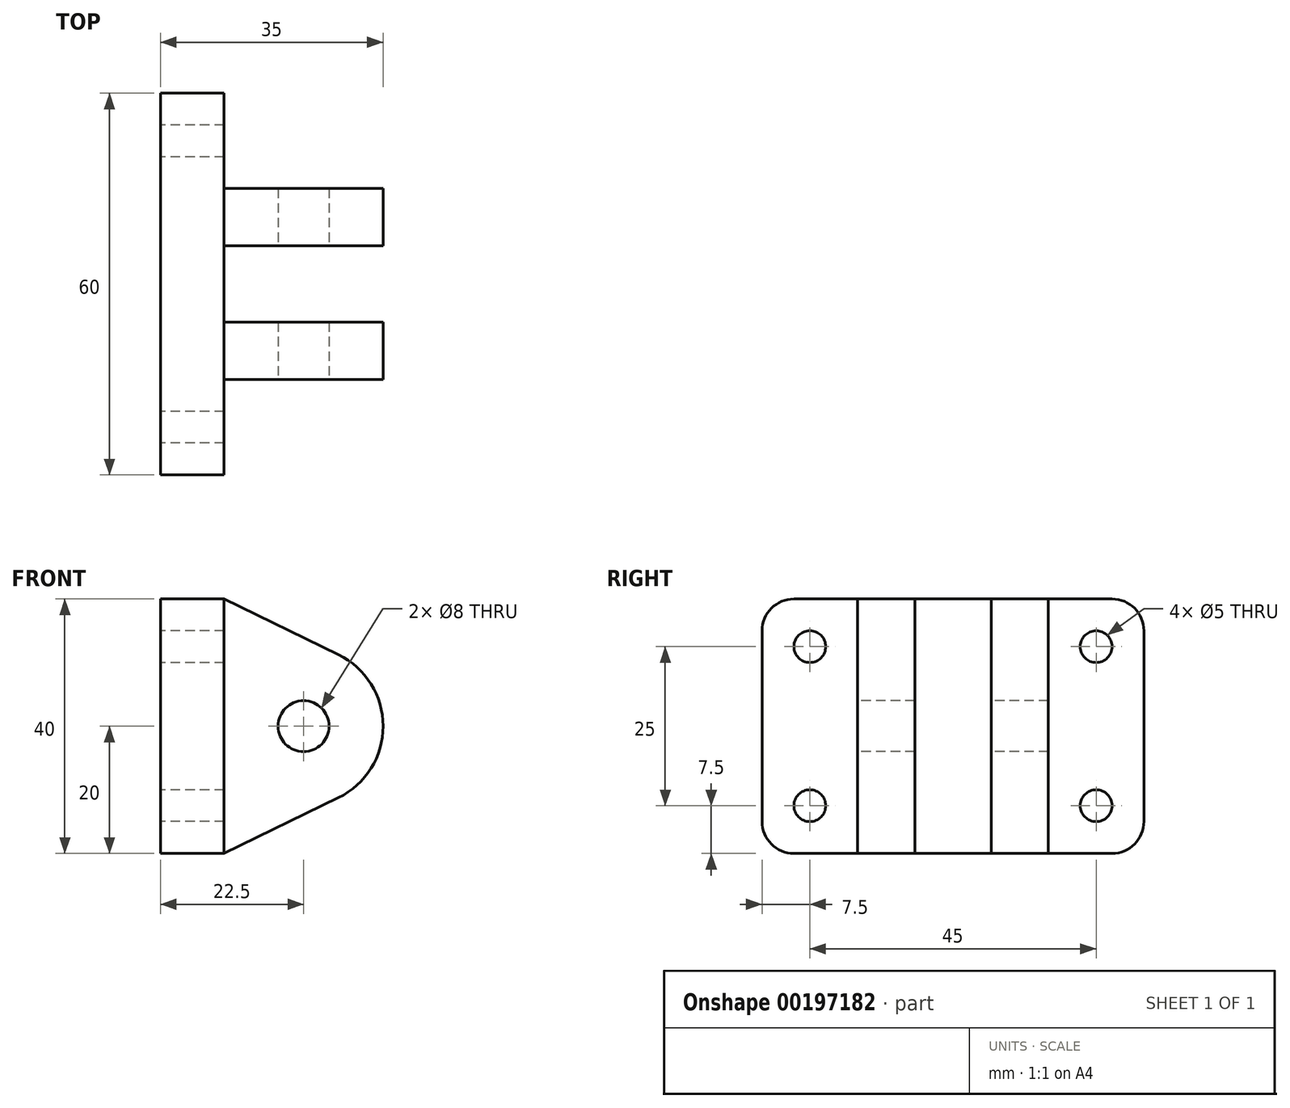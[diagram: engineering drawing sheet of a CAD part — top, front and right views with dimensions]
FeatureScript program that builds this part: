
annotation { "Feature Type Name" : "Feature", "Feature Type Description" : "" }
export const myFeature = defineFeature(function(context is Context, id is Id, definition is map)
    precondition{}
    {
        {
            var Q0;
            Q0=qCreatedBy(makeId("Right.planeOp"),FACE);
            var sketch = newSketch(context, id + "F0", { "sketchPlane" : qUnion([Q0])});
            skLineSegment(sketch, "E0.bottom", {"start": v(-25, 20) * mm, "end": v(25, 20) * mm});
            skLineSegment(sketch, "E0.top", {"start": v(-25, -20) * mm, "end": v(25, -20) * mm});
            skLineSegment(sketch, "E0.left", {"start": v(-30, 15) * mm, "end": v(-30, -15) * mm});
            skLineSegment(sketch, "E0.right", {"start": v(30, 15) * mm, "end": v(30, -15) * mm});
            skPoint(sketch, "E0.middle", {"position": v(0, 0) * mm});
            skLineSegment(sketch, "E1.bottom", {"start": v(-22.5, 12.5) * mm, "end": v(22.5, 12.5) * mm, "construction": true});
            skLineSegment(sketch, "E1.top", {"start": v(-22.5, -12.5) * mm, "end": v(22.5, -12.5) * mm, "construction": true});
            skLineSegment(sketch, "E1.left", {"start": v(-22.5, 12.5) * mm, "end": v(-22.5, -12.5) * mm, "construction": true});
            skLineSegment(sketch, "E1.right", {"start": v(22.5, 12.5) * mm, "end": v(22.5, -12.5) * mm, "construction": true});
            skCircle(sketch, "E2", {"center": v(-22.5, 12.5) * mm, "radius": 2.5 * mm});
            skCircle(sketch, "E3", {"center": v(22.5, 12.5) * mm, "radius": 2.5 * mm});
            skCircle(sketch, "E4", {"center": v(22.5, -12.5) * mm, "radius": 2.5 * mm});
            skCircle(sketch, "E5", {"center": v(-22.5, -12.5) * mm, "radius": 2.5 * mm});
            skPoint(sketch, "E6.visualSharp", {"position": v(-30, 20) * mm});
            skArc(sketch, "E6.filletArc", {"start": v(-25, 20) * mm, "mid": v(-28.54, 18.54) * mm, "end": v(-30, 15) * mm});
            skPoint(sketch, "E7.visualSharp", {"position": v(-30, -20) * mm});
            skArc(sketch, "E7.filletArc", {"start": v(-30, -15) * mm, "mid": v(-28.54, -18.54) * mm, "end": v(-25, -20) * mm});
            skPoint(sketch, "E8.visualSharp", {"position": v(30, -20) * mm});
            skArc(sketch, "E8.filletArc", {"start": v(25, -20) * mm, "mid": v(28.54, -18.54) * mm, "end": v(30, -15) * mm});
            skPoint(sketch, "E9.visualSharp", {"position": v(30, 20) * mm});
            skArc(sketch, "E9.filletArc", {"start": v(30, 15) * mm, "mid": v(28.54, 18.54) * mm, "end": v(25, 20) * mm});
            skSolve(sketch);
        }
        {
            var Q0;
            Q0=makeQuery(id+"F0.imprint","IMPRINT",FACE,{"disambiguationData":[TD([[makeQuery(id+"F0.imprint","IMPRINT",EDGE,{"derivedFrom":sQuery(id+"F0.wireOp",EDGE,"E0.bottom")}),-1.0]])]});
            extrude(context, id + "F1", {"entities" : qUnion([Q0]), "depth" : 10 * mm});
        }
        {
            var Q0;
            Q0=makeQuery(id+"F1.opExtrude","CAP_FACE",FACE,{"disambiguationData":[OSD([sQuery(id+"F0.wireOp",EDGE,"E0.bottom"),sQuery(id+"F0.wireOp",EDGE,"E0.top"),sQuery(id+"F0.wireOp",EDGE,"E0.left"),sQuery(id+"F0.wireOp",EDGE,"E0.right"),sQuery(id+"F0.wireOp",EDGE,"E2"),sQuery(id+"F0.wireOp",EDGE,"E3"),sQuery(id+"F0.wireOp",EDGE,"E4"),sQuery(id+"F0.wireOp",EDGE,"E5")])],"isStart":false});
            var sketch = newSketch(context, id + "F2", { "sketchPlane" : qUnion([Q0])});
            skLineSegment(sketch, "E10.bottom", {"start": v(-15, 20) * mm, "end": v(15, 20) * mm});
            skLineSegment(sketch, "E10.top", {"start": v(-15, -20) * mm, "end": v(15, -20) * mm});
            skLineSegment(sketch, "E10.left", {"start": v(-15, 20) * mm, "end": v(-15, -20) * mm});
            skLineSegment(sketch, "E10.right", {"start": v(15, 20) * mm, "end": v(15, -20) * mm});
            skSolve(sketch);
        }
        {
            var Q0;
            Q0=makeQuery(id+"F2.imprint","IMPRINT",FACE,{"disambiguationData":[TD([[makeQuery(id+"F2.imprint","IMPRINT",EDGE,{"derivedFrom":sQuery(id+"F2.wireOp",EDGE,"E10.bottom")}),-1.0]])]});
            extrude(context, id + "F3", {"entities" : qUnion([Q0]), "operationType" : NewBodyOperationType.ADD, "depth" : 25 * mm});
        }
        {
            var Q0;
            Q0=makeQuery(id+"F3.opExtrude","SWEPT_FACE",FACE,{"disambiguationData":[OSD([sQuery(id+"F2.wireOp",EDGE,"E10.left")])]});
            var sketch = newSketch(context, id + "F4", { "sketchPlane" : qUnion([Q0])});
            skArc(sketch, "E11", {"start": v(27.98, -11.24) * mm, "mid": v(35, 0) * mm, "end": v(27.98, 11.24) * mm});
            skLineSegment(sketch, "E12", {"start": v(27.98, 11.24) * mm, "end": v(10, 20) * mm});
            skLineSegment(sketch, "E13", {"start": v(10, -20) * mm, "end": v(27.98, -11.24) * mm});
            skLineSegment(sketch, "E14", {"start": v(10, -20) * mm, "end": v(35, -20) * mm});
            skLineSegment(sketch, "E15", {"start": v(35, -20) * mm, "end": v(35, 20) * mm});
            skLineSegment(sketch, "E16", {"start": v(35, 20) * mm, "end": v(10, 20) * mm});
            skCircle(sketch, "E17", {"center": v(22.5, 0) * mm, "radius": 4 * mm});
            skSolve(sketch);
        }
        {
            var Q0;
            Q0 = qSketchRegion(id + "F4", true);
            extrude(context, id + "F5", {"entities" : qUnion([Q0]), "operationType" : NewBodyOperationType.REMOVE, "oppositeDirection" : true, "depth" : 30 * mm});
        }
        {
            var Q0;
            Q0=makeQuery(id+"F3.boolean.opBoolean","MERGE",FACE,{"derivedFrom":[makeQuery(id+"F1.opExtrude","SWEPT_FACE",FACE,{"disambiguationData":[OSD([sQuery(id+"F0.wireOp",EDGE,"E0.bottom")])]}),makeQuery(id+"F3.opExtrude","SWEPT_FACE",FACE,{"disambiguationData":[OSD([sQuery(id+"F2.wireOp",EDGE,"E10.bottom")])]})]});
            var sketch = newSketch(context, id + "F6", { "sketchPlane" : qUnion([Q0])});
            skLineSegment(sketch, "E18.bottom", {"start": v(10, 6) * mm, "end": v(40, 6) * mm});
            skLineSegment(sketch, "E18.top", {"start": v(10, -6) * mm, "end": v(40, -6) * mm});
            skLineSegment(sketch, "E18.left", {"start": v(10, 6) * mm, "end": v(10, -6) * mm});
            skLineSegment(sketch, "E18.right", {"start": v(40, 6) * mm, "end": v(40, -6) * mm});
            skPoint(sketch, "E18.middle", {"position": v(25, 0) * mm});
            skSolve(sketch);
        }
        {
            var Q0;
            Q0 = qSketchRegion(id + "F6", true);
            extrude(context, id + "F7", {"entities" : qUnion([Q0]), "operationType" : NewBodyOperationType.REMOVE, "endBound" : BoundingType.THROUGH_ALL, "oppositeDirection" : true, "depth" : 25 * mm});
        }
    });
